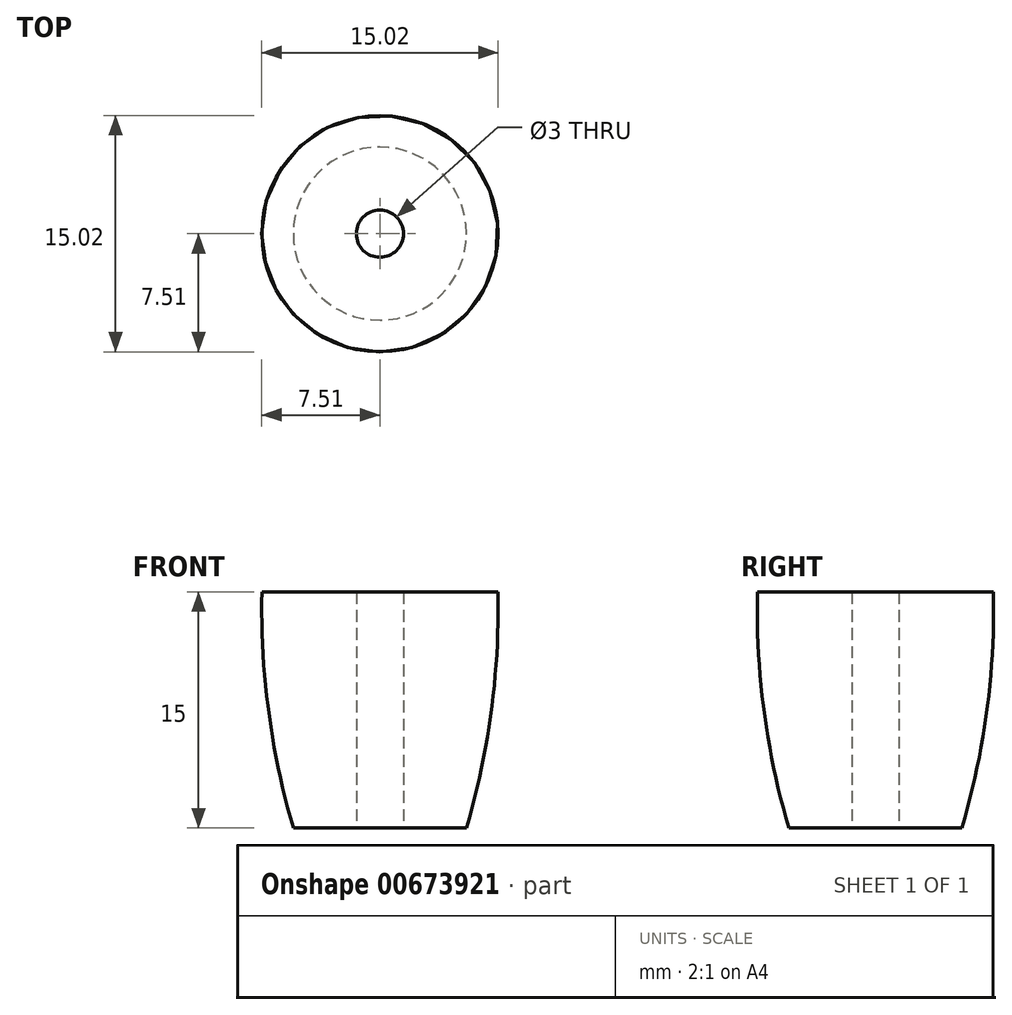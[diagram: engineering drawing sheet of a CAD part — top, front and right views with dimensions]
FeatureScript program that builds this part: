
annotation { "Feature Type Name" : "Feature", "Feature Type Description" : "" }
export const myFeature = defineFeature(function(context is Context, id is Id, definition is map)
    precondition{}
    {
        {
            var Q0;
            Q0=qCreatedBy(makeId("Front.planeOp"),FACE);
            var sketch = newSketch(context, id + "F0", { "sketchPlane" : qUnion([Q0])});
            skLineSegment(sketch, "E0", {"start": v(0, 0) * mm, "end": v(0, -15) * mm});
            skLineSegment(sketch, "E1", {"start": v(0, -15) * mm, "end": v(1.5, -15) * mm});
            skLineSegment(sketch, "E2", {"start": v(1.5, -15) * mm, "end": v(5.5, -15) * mm});
            skLineSegment(sketch, "E3", {"start": v(0, 0) * mm, "end": v(7.5, 0) * mm});
            skArc(sketch, "E4", {"start": v(5.5, -15) * mm, "mid": v(7.07, -7.58) * mm, "end": v(7.5, 0) * mm});
            skLineSegment(sketch, "E5.MirrorCS", {"start": v(0, 0) * mm, "end": v(0, 15) * mm});
            skArc(sketch, "E6.MirrorCS", {"start": v(5.5, 15) * mm, "mid": v(7.07, 7.58) * mm, "end": v(7.5, 0) * mm});
            skLineSegment(sketch, "E7.MirrorCS", {"start": v(1.5, 15) * mm, "end": v(5.5, 15) * mm});
            skLineSegment(sketch, "E8.MirrorCS", {"start": v(0, 15) * mm, "end": v(1.5, 15) * mm});
            skLineSegment(sketch, "E9", {"start": v(1.5, 15) * mm, "end": v(1.5, -15) * mm});
            skSolve(sketch);
        }
        {
            var Q0;
            {var subQ0=sQuery(id+"F0.wireOp",EDGE,"E6.MirrorCS");Q0=makeQuery(id+"F0.imprint","IMPRINT",FACE,{"disambiguationData":[TD([[makeQuery(id+"F0.imprint","IMPRINT",EDGE,{"derivedFrom":subQ0}),-1.0]])]});}
            var Q1;
            {var subQ0=sQuery(id+"F0.wireOp",EDGE,"E2");Q1=makeQuery(id+"F0.imprint","IMPRINT",FACE,{"disambiguationData":[TD([[makeQuery(id+"F0.imprint","IMPRINT",EDGE,{"derivedFrom":subQ0}),1.0]])]});}
            var Q2;
            Q2=sQuery(id+"F0.wireOp",EDGE,"E5.MirrorCS");
            revolve(context, id + "F1", {"entities" : qUnion([Q0, Q1]), "axis" : qUnion([Q2]), "revolveType" : RevolveType.FULL});
        }
    });
